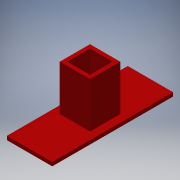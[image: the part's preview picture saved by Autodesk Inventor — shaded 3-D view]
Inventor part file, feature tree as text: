
AUTODESK INVENTOR PART (.ipt)
format: ipt  version: 2016 (Build 200138000, 138)  size: 115,712 bytes
history: native  units: in
note: dims shown in document units (in); Inventor stores cm internally (conversion verified against a paired STEP export)
features: extrude x3, sketch x2
ambient origin geometry x8: Origin, YZ Plane, XZ Plane, XY Plane, X Axis, Y Axis, Z Axis, Center Point
bodies: Solid1 (feature_tree)
feature tree (5):
  extrude  "Extrusion1"  Depth=4.0in
  sketch  "Sketch3"  dims[d2=0.125in d3=0.0in d8=1.0in d9=1.0in d10=0.25in d11=1.5in d12=0.125in d13=1.5in d14=0.0in d15=0.2in d16=0.5in d17=0.5in d20=0.125in d21=0.0in]
  extrude  "Extrusion3"  Depth=1.0in
  extrude  "Extrusion5"  Depth=1.0in
  sketch  "Sketch1"  dims[d0=1.5in d1=4.0in]
